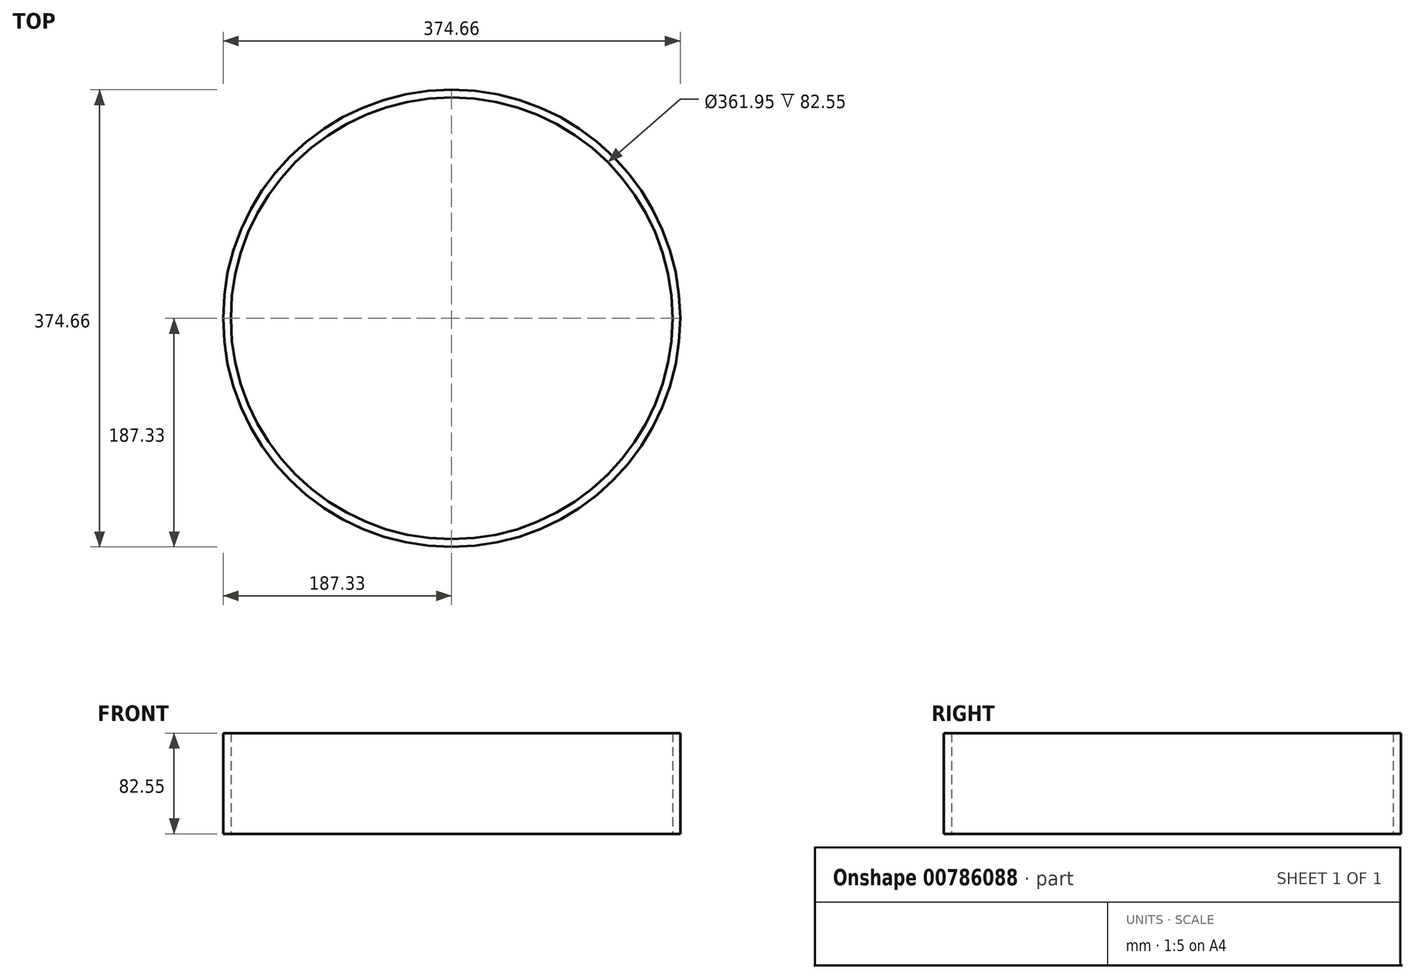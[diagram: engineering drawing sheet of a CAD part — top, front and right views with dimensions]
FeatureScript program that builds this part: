
annotation { "Feature Type Name" : "Feature", "Feature Type Description" : "" }
export const myFeature = defineFeature(function(context is Context, id is Id, definition is map)
    precondition{}
    {
        {
            var Q0;
            Q0=qCreatedBy(makeId("Top.planeOp"),FACE);
            var sketch = newSketch(context, id + "F0", { "sketchPlane" : qUnion([Q0])});
            skCircle(sketch, "E0", {"center": v(0, 0) * mm, "radius": 180.98 * mm});
            skCircle(sketch, "E1", {"center": v(0, 0) * mm, "radius": 187.33 * mm});
            skSolve(sketch);
        }
        {
            var Q0;
            Q0=qSketchRegion(id+"F0",true);
            extrude(context, id + "F1", {"entities" : qUnion([Q0]), "depth" : 82.55 * mm, "offsetDistance" : 25.4 * mm});
        }
    });
